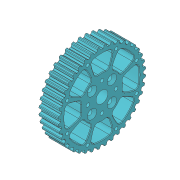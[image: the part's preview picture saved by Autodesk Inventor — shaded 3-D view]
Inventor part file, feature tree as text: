
AUTODESK INVENTOR PART (.ipt)
format: ipt  version: 2019.4 (Build 234330000, 330)  size: 640,000 bytes
history: native  units: mm
features: sketch x9, extrude x6, hole x4, fillet x2, pattern_circular x2, other x1, chamfer x1
ambient origin geometry x8: Origin, YZ Plane, XZ Plane, XY Plane, X Axis, Y Axis, Z Axis, Center Point
bodies: Body1 (feature_tree)
feature tree (25):
  other  "ソリッド1"
  extrude  "押し出し1"  Depth=1.95mm
  fillet  "フィレット1"  Radius=1.975mm
  fillet  "フィレット2"  Radius=1.11mm
  pattern_circular  "円形状パターン1"  [2 undecoded]
  extrude  "押し出し6"  Depth=37.44mm
  extrude  "押し出し2"  Depth=38.2mm
  hole  "穴1"  [1 undecoded]
  hole  "穴2"  [1 undecoded]
  hole  "穴3"  [1 undecoded]
  extrude  "押し出し3"  Depth=0.28mm
  extrude  "押し出し4"  Depth=400.0mm TaperAngle=360.0deg
  sketch  "スケッチ8"
  extrude  "押し出し5"  Depth=15.0mm
  hole  "穴4"  [1 undecoded]
  chamfer  "面取り1"  Distance=12.0mm
  pattern_circular  "円形状パターン2"  Count=4 Angle=360.0deg
  sketch  "スケッチ1"
  sketch  "スケッチ2"
  sketch  "スケッチ3"
  sketch  "スケッチ4"
  sketch  "スケッチ5"
  sketch  "スケッチ6"
  sketch  "スケッチ7"
  sketch  "スケッチ9"
note: 6 required parameter values undecoded (feature->parameter linkage not recoverable at this tier; creation-order binding heuristic only, values carry confidence <= 0.55)
